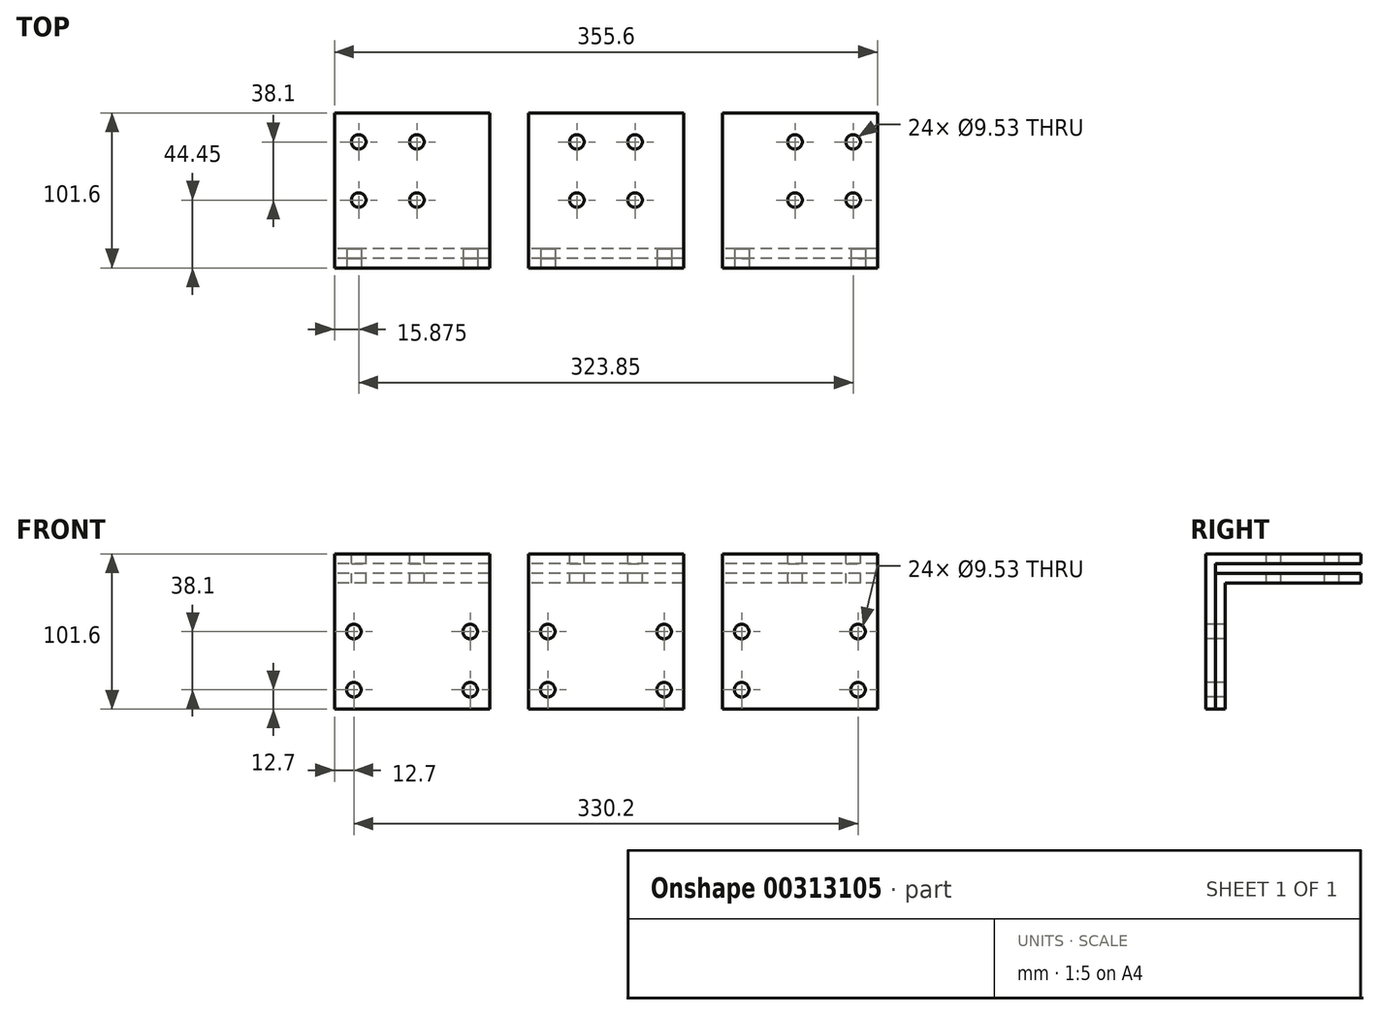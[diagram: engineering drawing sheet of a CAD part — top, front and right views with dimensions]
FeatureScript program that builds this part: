
annotation { "Feature Type Name" : "Feature", "Feature Type Description" : "" }
export const myFeature = defineFeature(function(context is Context, id is Id, definition is map)
    precondition{}
    {
        {
            var Q0;
            Q0=qCreatedBy(makeId("Right.planeOp"),FACE);
            var sketch = newSketch(context, id + "F0", { "sketchPlane" : qUnion([Q0])});
            skLineSegment(sketch, "E0", {"start": v(0, 0) * mm, "end": v(0, 101.6) * mm});
            skLineSegment(sketch, "E1", {"start": v(0, 101.6) * mm, "end": v(101.6, 101.6) * mm});
            skLineSegment(sketch, "E2", {"start": v(101.6, 101.6) * mm, "end": v(101.6, 95.25) * mm});
            skLineSegment(sketch, "E3", {"start": v(101.6, 95.25) * mm, "end": v(6.35, 95.25) * mm});
            skLineSegment(sketch, "E4", {"start": v(6.35, 95.25) * mm, "end": v(6.35, 0) * mm});
            skLineSegment(sketch, "E5", {"start": v(6.35, 0) * mm, "end": v(0, 0) * mm});
            skSolve(sketch);
        }
        {
            var Q0;
            Q0 = qSketchRegion(id + "F0", true);
            extrude(context, id + "F1", {"entities" : qUnion([Q0]), "endBound" : BoundingType.SYMMETRIC, "depth" : 355.6 * mm});
        }
        {
            var Q0;
            Q0=qCreatedBy(makeId("Right.planeOp"),FACE);
            var sketch = newSketch(context, id + "F2", { "sketchPlane" : qUnion([Q0])});
            skLineSegment(sketch, "E6", {"start": v(6.35, 0) * mm, "end": v(12.7, 0) * mm});
            skLineSegment(sketch, "E7", {"start": v(12.7, 0) * mm, "end": v(12.7, 82.55) * mm});
            skLineSegment(sketch, "E8", {"start": v(12.7, 82.55) * mm, "end": v(101.6, 82.55) * mm});
            skLineSegment(sketch, "E9", {"start": v(101.6, 82.55) * mm, "end": v(101.6, 88.9) * mm});
            skLineSegment(sketch, "E10", {"start": v(6.35, 0) * mm, "end": v(6.35, 88.9) * mm});
            skLineSegment(sketch, "E11", {"start": v(6.35, 88.9) * mm, "end": v(101.6, 88.9) * mm});
            skSolve(sketch);
        }
        {
            var Q0;
            Q0 = qSketchRegion(id + "F2", true);
            extrude(context, id + "F3", {"entities" : qUnion([Q0]), "endBound" : BoundingType.SYMMETRIC, "depth" : 355.6 * mm});
        }
        {
            var Q0;
            Q0=makeQuery(id+"F1.opExtrude","SWEPT_FACE",FACE,{"disambiguationData":[OSD([sQuery(id+"F0.wireOp",EDGE,"E0")])]});
            var sketch = newSketch(context, id + "F4", { "sketchPlane" : qUnion([Q0])});
            skLineSegment(sketch, "E12.bottom", {"start": v(-76.2, 0) * mm, "end": v(-50.8, 0) * mm});
            skLineSegment(sketch, "E12.top", {"start": v(-76.2, 101.6) * mm, "end": v(-50.8, 101.6) * mm});
            skLineSegment(sketch, "E12.left", {"start": v(-76.2, 0) * mm, "end": v(-76.2, 101.6) * mm});
            skLineSegment(sketch, "E12.right", {"start": v(-50.8, 0) * mm, "end": v(-50.8, 101.6) * mm});
            skLineSegment(sketch, "E13.bottom", {"start": v(50.8, 0) * mm, "end": v(76.2, 0) * mm});
            skLineSegment(sketch, "E13.top", {"start": v(50.8, 101.6) * mm, "end": v(76.2, 101.6) * mm});
            skLineSegment(sketch, "E13.left", {"start": v(50.8, 0) * mm, "end": v(50.8, 101.6) * mm});
            skLineSegment(sketch, "E13.right", {"start": v(76.2, 0) * mm, "end": v(76.2, 101.6) * mm});
            skCircle(sketch, "E14", {"center": v(-165.1, 12.7) * mm, "radius": 4.76 * mm});
            skCircle(sketch, "E15", {"center": v(-165.1, 50.8) * mm, "radius": 4.76 * mm});
            skCircle(sketch, "E16", {"center": v(-88.9, 50.8) * mm, "radius": 4.76 * mm});
            skCircle(sketch, "E17", {"center": v(-88.9, 12.7) * mm, "radius": 4.76 * mm});
            skCircle(sketch, "E18.1.0.0", {"center": v(-38.1, 50.8) * mm, "radius": 4.76 * mm});
            skCircle(sketch, "E18.1.0.1", {"center": v(-38.1, 12.7) * mm, "radius": 4.76 * mm});
            skCircle(sketch, "E18.1.0.2", {"center": v(38.1, 50.8) * mm, "radius": 4.76 * mm});
            skCircle(sketch, "E18.1.0.3", {"center": v(38.1, 12.7) * mm, "radius": 4.76 * mm});
            skCircle(sketch, "E18.2.0.0", {"center": v(88.9, 50.8) * mm, "radius": 4.76 * mm});
            skCircle(sketch, "E18.2.0.1", {"center": v(88.9, 12.7) * mm, "radius": 4.76 * mm});
            skCircle(sketch, "E18.2.0.2", {"center": v(165.1, 50.8) * mm, "radius": 4.76 * mm});
            skCircle(sketch, "E18.2.0.3", {"center": v(165.1, 12.7) * mm, "radius": 4.76 * mm});
            skLineSegment(sketch, "E18.direction1", {"start": v(-165.1, 12.7) * mm, "end": v(-38.1, 12.7) * mm, "construction": true});
            skSolve(sketch);
        }
        {
            var Q0;
            Q0 = qSketchRegion(id + "F4", true);
            extrude(context, id + "F5", {"entities" : qUnion([Q0]), "operationType" : NewBodyOperationType.REMOVE, "endBound" : BoundingType.THROUGH_ALL, "oppositeDirection" : true, "depth" : 25.4 * mm});
        }
        {
            var Q0;
            {var subQ2=sQuery(id+"F0.wireOp",EDGE,"E1");Q0=makeQuery(id+"F5.boolean.opBoolean","SPLIT",FACE,{"disambiguationData":[TD([makeQuery(id+"F5.opExtrude","SWEPT_FACE",FACE,{"disambiguationData":[OSD([sQuery(id+"F4.wireOp",EDGE,"E12.left")])]})])],"derivedFrom":makeQuery(id+"F1.opExtrude","SWEPT_FACE",FACE,{"disambiguationData":[OSD([subQ2])]})});}
            var sketch = newSketch(context, id + "F6", { "sketchPlane" : qUnion([Q0])});
            skCircle(sketch, "E19", {"center": v(-161.92, 82.55) * mm, "radius": 4.76 * mm});
            skCircle(sketch, "E20", {"center": v(-123.83, 82.55) * mm, "radius": 4.76 * mm});
            skCircle(sketch, "E21", {"center": v(-123.83, 44.45) * mm, "radius": 4.76 * mm});
            skCircle(sketch, "E22", {"center": v(-161.92, 44.45) * mm, "radius": 4.76 * mm});
            skCircle(sketch, "E23.1.0.0", {"center": v(-19.05, 82.55) * mm, "radius": 4.76 * mm});
            skCircle(sketch, "E23.1.0.1", {"center": v(19.05, 44.45) * mm, "radius": 4.76 * mm});
            skCircle(sketch, "E23.1.0.2", {"center": v(19.05, 82.55) * mm, "radius": 4.76 * mm});
            skCircle(sketch, "E23.1.0.3", {"center": v(-19.05, 44.45) * mm, "radius": 4.76 * mm});
            skCircle(sketch, "E23.2.0.0", {"center": v(123.83, 82.55) * mm, "radius": 4.76 * mm});
            skCircle(sketch, "E23.2.0.1", {"center": v(161.93, 44.45) * mm, "radius": 4.76 * mm});
            skCircle(sketch, "E23.2.0.2", {"center": v(161.93, 82.55) * mm, "radius": 4.76 * mm});
            skCircle(sketch, "E23.2.0.3", {"center": v(123.83, 44.45) * mm, "radius": 4.76 * mm});
            skLineSegment(sketch, "E23.direction1", {"start": v(-161.92, 44.45) * mm, "end": v(-19.05, 44.45) * mm, "construction": true});
            skSolve(sketch);
        }
        {
            var Q0;
            Q0 = qSketchRegion(id + "F6", true);
            extrude(context, id + "F7", {"entities" : qUnion([Q0]), "operationType" : NewBodyOperationType.REMOVE, "endBound" : BoundingType.THROUGH_ALL, "oppositeDirection" : true, "depth" : 25.4 * mm});
        }
    });
